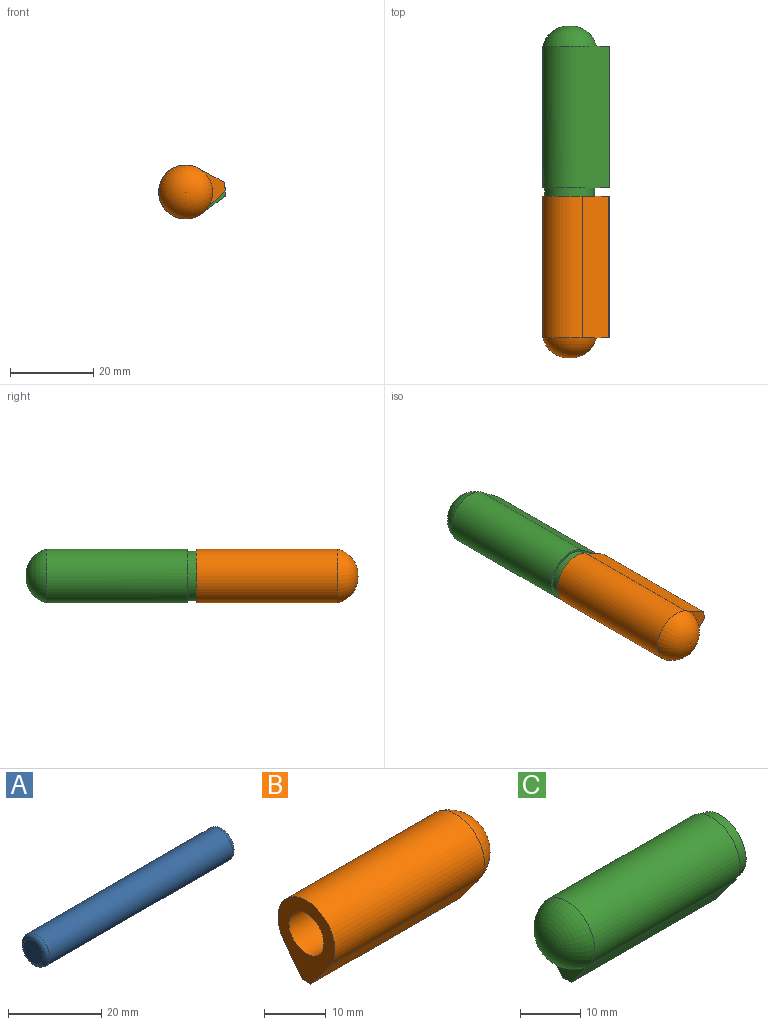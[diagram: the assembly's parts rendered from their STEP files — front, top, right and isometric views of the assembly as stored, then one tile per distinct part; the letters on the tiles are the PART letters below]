
ASSEMBLY  parts=3 mates=2
PART A: 5 faces, bbox 57.6x8.7x8.7 mm
  f0: plane 6x6mm, normal (-1,0,0), area 28.3mm2, adj f1
  f1: torus R=3mm, axis (1,0,0), area 35.9mm2, adj f0,f2
  f2: cylinder r=4mm len=55.6mm, axis (1,0,0), area 1397.4mm2, adj f1,f3
  f3: torus R=3mm, axis (1,0,0), area 35.9mm2, adj f2,f4
  f4: plane 6x6mm, normal (1,0,0), area 28.3mm2, adj f3
PART B: 9 faces, bbox 39.2x13x16 mm
  f0: plane 16x13mm, normal (-1,0,0), area 98.3mm2, adj f1,f2,f3,f4,f7
  f1: plane 34.13x5.6mm, normal (0,0.8,-0.6), area 238.9mm2, adj f0,f2,f4,f5
  f2: cylinder r=6.5mm len=34.13mm, axis (-1,0,0), area 982.3mm2, adj f0,f1,f3,f6
  f3: plane 34.13x5.6mm, normal (0,-0.8,-0.6), area 238.9mm2, adj f0,f2,f4,f5
  f4: plane 34.13x2mm, normal (0,0,-1), area 68.2mm2, adj f0,f1,f3,f5
  f5: plane 10.4x5.6mm, normal (1,0,0), area 15.8mm2, adj f1,f3,f4,f6
  f6: torus R=0.21mm, axis (1,0,0), area 210.4mm2, adj f2,f5
  f7: cylinder r=4mm len=28.8mm, axis (1,0,0), area 723.8mm2, adj f0,f8
  f8: cone r=4mm half-angle=60deg, axis (-1,0,0), area 58mm2, adj f7
PART C: 11 faces, bbox 41.2x13x16 mm
  f0: cylinder r=6mm len=12mm, axis (1,0,0), area 75.4mm2, adj f1,f7
  f1: plane 12x12mm, normal (1,0,0), area 62.8mm2, adj f0,f10
  f2: plane 10.4x5.6mm, normal (-1,0,0), area 15.8mm2, adj f3,f5,f6,f8
  f3: plane 34.13x5.6mm, normal (0,0.8,-0.6), area 238.9mm2, adj f2,f4,f6,f7
  f4: cylinder r=6.5mm len=34.13mm, axis (1,0,0), area 982.3mm2, adj f3,f5,f7,f8
  f5: plane 34.13x5.6mm, normal (0,-0.8,-0.6), area 238.9mm2, adj f2,f4,f6,f7
  f6: plane 34.13x2mm, normal (0,0,-1), area 68.2mm2, adj f2,f3,f5,f7
  f7: plane 16x13mm, normal (1,0,0), area 35.5mm2, adj f0,f3,f4,f5,f6
  f8: torus R=0.21mm, axis (1,0,0), area 210.4mm2, adj f2,f4
  f9: cone r=0mm half-angle=60deg, axis (1,0,0), area 58mm2, adj f10
  f10: cylinder r=4mm len=30.8mm, axis (1,0,0), area 774.1mm2, adj f1,f9
PLACE A rot(axis=(0.58,-0.58,-0.58),120deg) t=(0,-1,0)mm fixed
PLACE B rot(axis=(0.6,-0.6,-0.52),124.8deg) t=(0,1,0)mm
PLACE C rot(axis=(0.58,-0.58,-0.58),120deg) t=(0,1,0)mm
MATE fastened C.f9 <-> A.f1  axis (0,-1,0) through (0,1,0)mm
MATE revolute C.f9 <-> B.f6  axis (0,-1,0) through (0,1,0)mm
